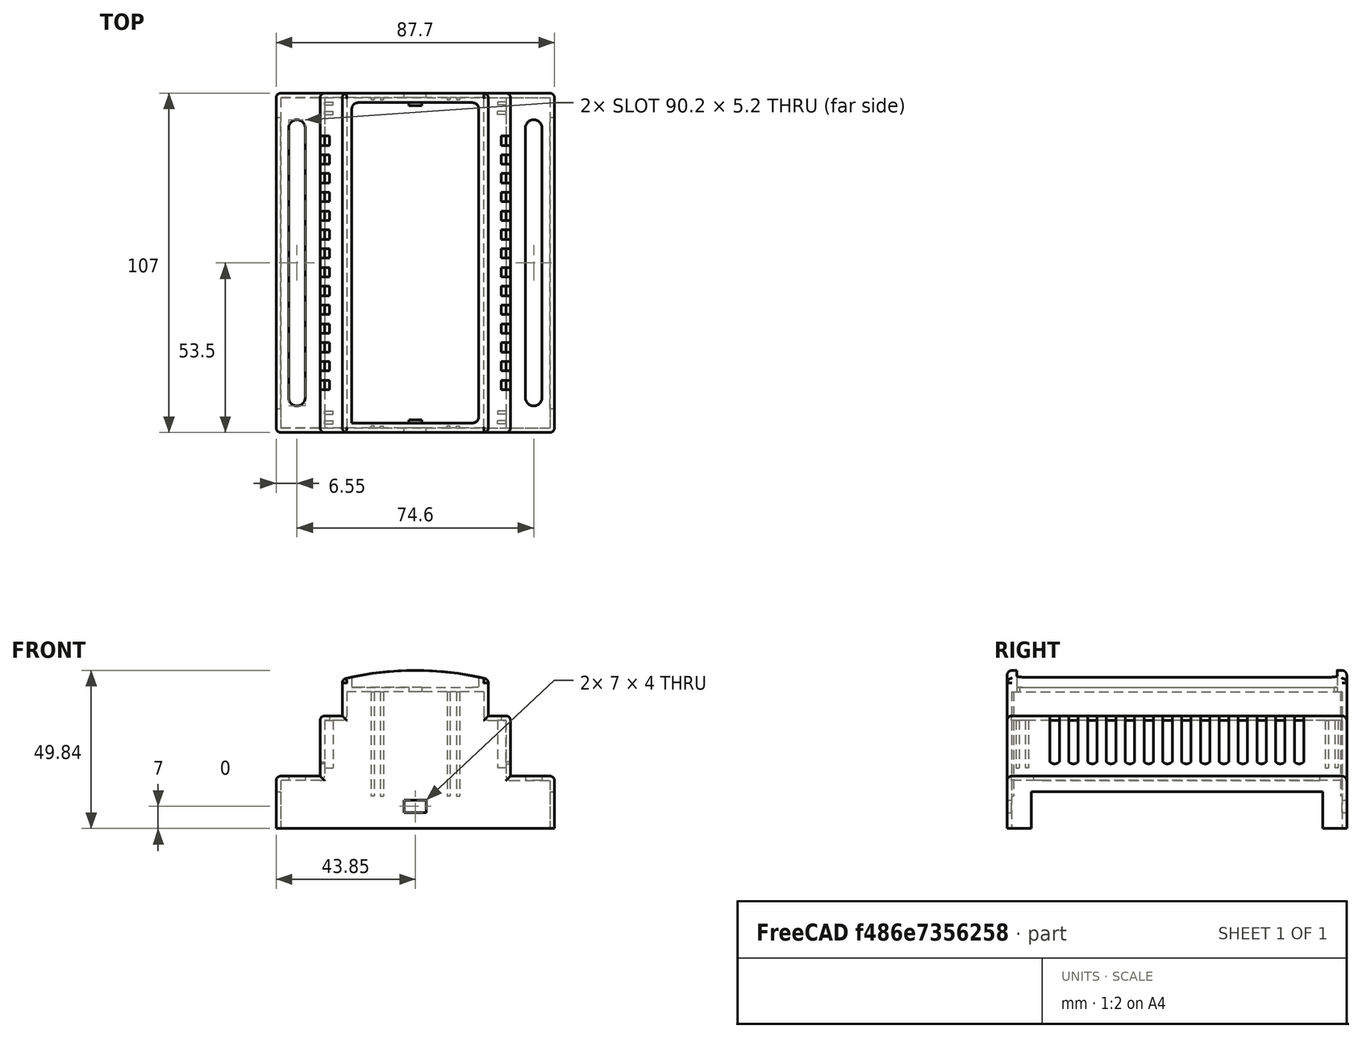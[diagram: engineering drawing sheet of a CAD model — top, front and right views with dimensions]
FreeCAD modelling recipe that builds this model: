
FCSTD DOCUMENT  (FreeCAD 1.0R39109 (Git))
Label: Parte Superior
License: All rights reserved
LicenseURL: https://en.wikipedia.org/wiki/All_rights_reserved
objects: Sketcher::SketchObject×15, PartDesign::Pad×9, PartDesign::Mirrored×7, PartDesign::Pocket×6, PartDesign::Fillet×4, PartDesign::Thickness×2, PartDesign::Plane×1, PartDesign::Body×1
note: 109 computed .brp shape members not serialized (recipe doc carries the construction recipe); baked Part::Feature solids carry a one-line shape summary decoded from their .brp

FEATURE [Sketcher::SketchObject] Sketch
  ArcFitTolerance = 1e-06
  AttachmentSupport = -> [XZ_Plane001]
  FullyConstrained = true
  MakeInternals = false
  MapMode = 5
  Placement = pos=(0,0,0) rot=(1,0,0;1.5708rad)
  sketch-geometry (12):
    g0: LineSegment StartX=-43.85 StartY=0 StartZ=0 EndX=43.85 EndY=0 EndZ=0
    g1: LineSegment StartX=-43.85 StartY=0 StartZ=0 EndX=-43.85 EndY=16.54 EndZ=0
    g2: LineSegment StartX=43.85 StartY=0 StartZ=0 EndX=43.85 EndY=16.54 EndZ=0
    g3: LineSegment StartX=-43.85 StartY=16.54 StartZ=0 EndX=-30 EndY=16.54 EndZ=0
    g4: LineSegment StartX=43.85 StartY=16.54 StartZ=0 EndX=30 EndY=16.54 EndZ=0
    g5: LineSegment StartX=-30 StartY=16.54 StartZ=0 EndX=-30 EndY=35.54 EndZ=0
    g6: LineSegment StartX=30 StartY=16.54 StartZ=0 EndX=30 EndY=35.54 EndZ=0
    g7: LineSegment StartX=-30 StartY=35.54 StartZ=0 EndX=-23 EndY=35.54 EndZ=0
    g8: LineSegment StartX=30 StartY=35.54 StartZ=0 EndX=23 EndY=35.54 EndZ=0
    g9: LineSegment StartX=23 StartY=35.54 StartZ=0 EndX=23 EndY=44.54 EndZ=0
    g10: LineSegment StartX=-23 StartY=35.54 StartZ=0 EndX=-23 EndY=44.54 EndZ=0
    g11: LineSegment StartX=-23 StartY=44.54 StartZ=0 EndX=23 EndY=44.54 EndZ=0
  constraints (36):
    c: Distance(g0) = 87.7
    c: PointOnObject(g0,g-1)
    c: PointOnObject(g0,g-1)
    c: Vertical(g1)
    c: Coincident(g1,g0)
    c: Vertical(g2)
    c: Coincident(g2,g0)
    c: Distance(g3) = 13.85
    c: Horizontal(g3)
    c: Coincident(g3,g1)
    c: Distance(g4) = 13.85
    c: Horizontal(g4)
    c: Coincident(g4,g2)
    c: Vertical(g5)
    c: Coincident(g5,g3)
    c: Vertical(g6)
    c: Coincident(g6,g4)
    c: Distance(g7) = 7
    c: Horizontal(g7)
    c: Coincident(g7,g5)
    c: Distance(g8) = 7
    c: Horizontal(g8)
    c: Coincident(g8,g6)
    c: Vertical(g9)
    c: Coincident(g9,g8)
    c: Vertical(g10)
    c: Coincident(g10,g7)
    c: Coincident(g11,g10)
    c: Coincident(g11,g9)
    c: Equal(g1,g2)
    c: Equal(g5,g6)
    c: Equal(g10,g9)
    c: Distance(g0,g11) = 44.54
    c: DistanceY(g1,g1) = 16.54
    c: Distance(g5,g0) = 35.54
    c: Distance(g10,g-2) = 23
FEATURE [PartDesign::Pad] Pad
  Direction = (0,-1,2e-16)
  Length = 107
  Length2 = 10
  Placement = pos=(0,0,0) rot=(1,0,0;1.5708rad)
  Profile = -> Sketch
  ReferenceAxis = -> Sketch [N_Axis]
  Refine = true
  Suppressed = false
  Type = 0
FEATURE [PartDesign::Thickness] Thickness
  Base = -> Pad
  BaseFeature = -> Pad
  Intersection = false
  Join = 0
  Mode = 0
  Placement = pos=(0,0,0) rot=(1,0,0;1.5708rad)
  Refine = true
  Reversed = true
  SupportTransform = false
  Suppressed = false
  Value = 1.4
FEATURE [PartDesign::Thickness] Thickness001
  Base = -> Thickness [Face1]
  BaseFeature = -> Thickness
  Intersection = false
  Join = 0
  Mode = 0
  Refine = true
  Reversed = true
  SupportTransform = false
  Suppressed = false
  Value = 1.4
FEATURE [Sketcher::SketchObject] Sketch001
  ArcFitTolerance = 1e-06
  AttachmentSupport = -> [Thickness001]
  FullyConstrained = true
  MakeInternals = false
  MapMode = 5
  Placement = pos=(-43.85,0,0) rot=(0.57735,-0.57735,-0.57735;2.0944rad)
  sketch-geometry (4):
    g0: LineSegment StartX=7.575 StartY=0 StartZ=0 EndX=99.425 EndY=0 EndZ=0
    g1: LineSegment StartX=99.425 StartY=0 StartZ=0 EndX=99.425 EndY=11.6 EndZ=0
    g2: LineSegment StartX=99.425 StartY=11.6 StartZ=0 EndX=7.575 EndY=11.6 EndZ=0
    g3: LineSegment StartX=7.575 StartY=11.6 StartZ=0 EndX=7.575 EndY=0 EndZ=0
  constraints (12):
    c: Coincident(g0,g1)
    c: Coincident(g1,g2)
    c: Coincident(g2,g3)
    c: Coincident(g3,g0)
    c: Horizontal(g0)
    c: Horizontal(g2)
    c: Vertical(g1)
    c: Vertical(g3)
    c: PointOnObject(g0,g-1)
    c: DistanceX(g2,g2) = 91.85
    c: DistanceY(g1,g1) = 11.6
    c: DistanceX(g-1,g0) = 7.575
FEATURE [PartDesign::Pocket] Pocket
  BaseFeature = -> Thickness001
  Direction = (1,0,0)
  Length = 5
  Length2 = 5
  Profile = -> Sketch001
  ReferenceAxis = -> Sketch001 [N_Axis]
  Refine = true
  Suppressed = false
  Type = 1
FEATURE [Sketcher::SketchObject] Sketch002
  ArcFitTolerance = 1e-06
  AttachmentSupport = -> [Pocket]
  FullyConstrained = true
  MakeInternals = false
  MapMode = 5
  Placement = pos=(0,4.2e-15,0) rot=(0,0.707107,0.707107;3.14159rad)
  sketch-geometry (4):
    g0: LineSegment StartX=-23 StartY=44.54 StartZ=0 EndX=23 EndY=44.54 EndZ=0
    g1: LineSegment StartX=-23 StartY=44.54 StartZ=0 EndX=-23 EndY=47.04 EndZ=0
    g2: LineSegment StartX=23 StartY=44.54 StartZ=0 EndX=23 EndY=47.04 EndZ=0
    g3: ArcOfCircle CenterX=1.7e-15 CenterY=-46.0243 CenterZ=0 NormalX=0 NormalY=0 NormalZ=1 AngleXU=0 Radius=95.8643 StartAngle=1.32851 EndAngle=1.81308
  constraints (13):
    c: Distance(g0) = 46
    c: Horizontal(g0)
    c: Distance(g-1,g0) = 44.54
    c: Distance(g0,g-2) = 23
    c: Distance(g1) = 2.5
    c: Coincident(g1,g0)
    c: Vertical(g1)
    c: Distance(g2) = 2.5
    c: Coincident(g2,g0)
    c: Vertical(g2)
    c: Coincident(g3,g1)
    c: Coincident(g3,g2)
    c: Distance(g3,g0) = -5.3
FEATURE [PartDesign::Pad] Pad001
  BaseFeature = -> Pocket
  Direction = (0,1,-2e-16)
  Length = 107
  Length2 = 10
  Profile = -> Sketch002
  ReferenceAxis = -> Sketch002 [N_Axis]
  Refine = true
  Suppressed = false
  Type = 0
FEATURE [Sketcher::SketchObject] Sketch003
  ArcFitTolerance = 1e-06
  AttachmentSupport = -> [Pad001]
  ExternalGeometry = -> [Pad001]
  FullyConstrained = true
  MakeInternals = false
  MapMode = 5
  Placement = pos=(0,4.2e-15,0) rot=(0,0.707107,0.707107;3.14159rad)
  sketch-geometry (4):
    g0: LineSegment StartX=-23 StartY=44.54 StartZ=0 EndX=-23 EndY=47.04 EndZ=0
    g1: LineSegment StartX=23 StartY=44.54 StartZ=0 EndX=23 EndY=47.04 EndZ=0
    g2: ArcOfCircle CenterX=4.82e-14 CenterY=-46.0243 CenterZ=0 NormalX=0 NormalY=0 NormalZ=1 AngleXU=0 Radius=95.8643 StartAngle=1.32851 EndAngle=1.81308
    g3: LineSegment StartX=-23 StartY=44.54 StartZ=0 EndX=23 EndY=44.54 EndZ=0
  constraints (9):
    c: Distance(g0) = 2.5
    c: Coincident(g2,g0)
    c: Coincident(g2,g1)
    c: Coincident(g3,g-3)
    c: Coincident(g3,g-3)
    c: Perpendicular(g0,g3) = 4.71239
    c: Distance(g2,g3) = -5.3
    c: Perpendicular(g1,g3) = 4.71239
    c: DistanceY(g1,g1) = 2.5
FEATURE [PartDesign::Pad] Pad002
  BaseFeature = -> Pad001
  Direction = (0,1,-2e-16)
  Length = 3
  Length2 = 10
  Profile = -> Sketch003
  ReferenceAxis = -> Sketch003 [N_Axis]
  Refine = true
  Reversed = true
  Suppressed = false
  Type = 0
FEATURE [Sketcher::SketchObject] Sketch004
  ArcFitTolerance = 1e-06
  AttachmentSupport = -> [Pad002]
  ExternalGeometry = -> [Pad002]
  FullyConstrained = true
  MakeInternals = false
  MapMode = 5
  Placement = pos=(0,-107,0) rot=(1,0,0;1.5708rad)
  sketch-geometry (4):
    g0: LineSegment StartX=-23 StartY=44.54 StartZ=0 EndX=23 EndY=44.54 EndZ=0
    g1: LineSegment StartX=23 StartY=44.54 StartZ=0 EndX=23 EndY=47.04 EndZ=0
    g2: LineSegment StartX=-23 StartY=44.54 StartZ=0 EndX=-23 EndY=47.04 EndZ=0
    g3: ArcOfCircle CenterX=3.7756e-12 CenterY=-46.0243 CenterZ=0 NormalX=0 NormalY=0 NormalZ=1 AngleXU=0 Radius=95.8643 StartAngle=1.32851 EndAngle=1.81308
  constraints (9):
    c: Coincident(g0,g-5)
    c: Coincident(g0,g-6)
    c: Coincident(g1,g0)
    c: Coincident(g1,g-6)
    c: Coincident(g2,g0)
    c: Coincident(g2,g-5)
    c: Coincident(g3,g2)
    c: Coincident(g3,g1)
    c: Tangent(g3,g-4)
FEATURE [PartDesign::Pad] Pad003
  BaseFeature = -> Pad002
  Direction = (0,-1,2e-16)
  Length = 3
  Length2 = 10
  Profile = -> Sketch004
  ReferenceAxis = -> Sketch004 [N_Axis]
  Refine = true
  Reversed = true
  Suppressed = false
  Type = 0
FEATURE [Sketcher::SketchObject] Sketch005
  ArcFitTolerance = 1e-06
  AttachmentSupport = -> [Pad003]
  ExternalGeometry = -> [Pad003]
  FullyConstrained = true
  MakeInternals = false
  MapMode = 5
  Placement = pos=(23,-8.5e-15,1.304e-13) rot=(0.57735,0.57735,0.57735;2.0944rad)
  sketch-geometry (4):
    g0: LineSegment StartX=-104 StartY=49.84 StartZ=0 EndX=-104 EndY=44.54 EndZ=0
    g1: LineSegment StartX=-104 StartY=44.54 StartZ=0 EndX=-3 EndY=44.54 EndZ=0
    g2: LineSegment StartX=-3 StartY=49.84 StartZ=0 EndX=-3 EndY=44.54 EndZ=0
    g3: LineSegment StartX=-104 StartY=49.84 StartZ=0 EndX=-3 EndY=49.84 EndZ=0
  constraints (8):
    c: Coincident(g0,g-5)
    c: Coincident(g0,g-3)
    c: Coincident(g1,g0)
    c: Coincident(g1,g-3)
    c: Coincident(g2,g-4)
    c: Coincident(g2,g1)
    c: Coincident(g3,g0)
    c: Coincident(g3,g2)
FEATURE [PartDesign::Pad] Pad004
  BaseFeature = -> Pad003
  Direction = (1,0,5.8e-15)
  Length = 3
  Length2 = 10
  Profile = -> Sketch005
  ReferenceAxis = -> Sketch005 [N_Axis]
  Refine = true
  Reversed = true
  Suppressed = false
  Type = 0
FEATURE [PartDesign::Mirrored] Mirrored
  BaseFeature = -> Pad004
  MirrorPlane = -> YZ_Plane001
  Originals = -> [Pad004]
  Refine = true
  Suppressed = false
  TransformMode = 0
FEATURE [Sketcher::SketchObject] Sketch006
  ArcFitTolerance = 1e-06
  AttachmentSupport = -> [Mirrored]
  FullyConstrained = true
  MakeInternals = false
  MapMode = 5
  Placement = pos=(0,7.3e-15,16.54) rot=(0,0,1;0rad)
  sketch-geometry (4):
    g0: ArcOfCircle CenterX=37.3 CenterY=-11 CenterZ=0 NormalX=0 NormalY=0 NormalZ=1 AngleXU=0 Radius=2.6 StartAngle=2.2037e-12 EndAngle=3.14159
    g1: ArcOfCircle CenterX=37.3 CenterY=-96 CenterZ=0 NormalX=0 NormalY=0 NormalZ=1 AngleXU=0 Radius=2.6 StartAngle=3.14159 EndAngle=6.28319
    g2: LineSegment StartX=39.9 StartY=-11 StartZ=0 EndX=39.9 EndY=-96 EndZ=0
    g3: LineSegment StartX=34.7 StartY=-11 StartZ=0 EndX=34.7 EndY=-96 EndZ=0
  constraints (10):
    c: Tangent(g0,g2) = 1.5708
    c: Tangent(g0,g3) = -1.5708
    c: Tangent(g1,g2) = 1.5708
    c: Tangent(g1,g3) = -1.5708
    c: Equal(g0,g1)
    c: Vertical(g2)
    c: Distance(g2,g3) = 5.2
    c: DistanceY(g2,g2) = 85
    c: Distance(g0,g-2) = 37.3
    c: Distance(g0,g-1) = 11
FEATURE [PartDesign::Pocket] Pocket001
  BaseFeature = -> Mirrored
  Direction = (0,0,-1)
  Length = 5
  Length2 = 5
  Profile = -> Sketch006
  ReferenceAxis = -> Sketch006 [N_Axis]
  Refine = true
  Suppressed = false
  Type = 0
FEATURE [PartDesign::Mirrored] Mirrored001
  BaseFeature = -> Pocket001
  MirrorPlane = -> YZ_Plane001
  Originals = -> [Pocket001]
  Refine = true
  Suppressed = false
  TransformMode = 0
FEATURE [Sketcher::SketchObject] Sketch007
  ArcFitTolerance = 1e-06
  AttachmentSupport = -> [Mirrored001]
  ExternalGeometry = -> [Mirrored001]
  FullyConstrained = true
  MakeInternals = false
  MapMode = 5
  Placement = pos=(30,0,0) rot=(0.57735,0.57735,0.57735;2.0944rad)
  sketch-geometry (57):
    g0: LineSegment [constr] StartX=-53.5 StartY=35.54 StartZ=0 EndX=-53.5 EndY=16.54 EndZ=0
    g1: LineSegment StartX=-16.4625 StartY=35.54 StartZ=0 EndX=-13.4995 EndY=35.54 EndZ=0
    g2: LineSegment StartX=-13.4995 StartY=35.54 StartZ=0 EndX=-13.4995 EndY=21.04 EndZ=0
    g3: LineSegment StartX=-16.4625 StartY=35.54 StartZ=0 EndX=-16.4625 EndY=21.04 EndZ=0
    g4: ArcOfCircle CenterX=-14.981 CenterY=22.3836 CenterZ=0 NormalX=0 NormalY=0 NormalZ=1 AngleXU=0 Radius=2 StartAngle=3.8782 EndAngle=5.54658
    g5: LineSegment StartX=-22.3885 StartY=35.54 StartZ=0 EndX=-19.4255 EndY=35.54 EndZ=0
    g6: LineSegment StartX=-19.4255 StartY=35.54 StartZ=0 EndX=-19.4255 EndY=21.04 EndZ=0
    g7: LineSegment StartX=-22.3885 StartY=35.54 StartZ=0 EndX=-22.3885 EndY=21.04 EndZ=0
    g8: ArcOfCircle CenterX=-20.907 CenterY=22.3836 CenterZ=0 NormalX=0 NormalY=0 NormalZ=1 AngleXU=0 Radius=2 StartAngle=3.8782 EndAngle=5.54658
    g9: LineSegment StartX=-28.3145 StartY=35.54 StartZ=0 EndX=-25.3515 EndY=35.54 EndZ=0
    g10: LineSegment StartX=-25.3515 StartY=35.54 StartZ=0 EndX=-25.3515 EndY=21.04 EndZ=0
    g11: LineSegment StartX=-28.3145 StartY=35.54 StartZ=0 EndX=-28.3145 EndY=21.04 EndZ=0
    g12: ArcOfCircle CenterX=-26.833 CenterY=22.3836 CenterZ=0 NormalX=0 NormalY=0 NormalZ=1 AngleXU=0 Radius=2 StartAngle=3.8782 EndAngle=5.54658
    g13: LineSegment StartX=-34.2405 StartY=35.54 StartZ=0 EndX=-31.2775 EndY=35.54 EndZ=0
    g14: LineSegment StartX=-34.2405 StartY=35.54 StartZ=0 EndX=-34.2405 EndY=21.04 EndZ=0
    g15: LineSegment StartX=-31.2775 StartY=35.54 StartZ=0 EndX=-31.2775 EndY=21.04 EndZ=0
    g16: ArcOfCircle CenterX=-32.759 CenterY=22.3836 CenterZ=0 NormalX=0 NormalY=0 NormalZ=1 AngleXU=0 Radius=2 StartAngle=3.8782 EndAngle=5.54658
    g17: LineSegment StartX=-40.1665 StartY=35.54 StartZ=0 EndX=-37.2035 EndY=35.54 EndZ=0
    g18: LineSegment StartX=-37.2035 StartY=35.54 StartZ=0 EndX=-37.2035 EndY=21.04 EndZ=0
    g19: LineSegment StartX=-40.1665 StartY=35.54 StartZ=0 EndX=-40.1665 EndY=21.04 EndZ=0
    g20: ArcOfCircle CenterX=-38.685 CenterY=22.3836 CenterZ=0 NormalX=0 NormalY=0 NormalZ=1 AngleXU=0 Radius=2 StartAngle=3.8782 EndAngle=5.54658
    g21: LineSegment StartX=-46.0925 StartY=35.54 StartZ=0 EndX=-43.1295 EndY=35.54 EndZ=0
    g22: LineSegment StartX=-43.1295 StartY=35.54 StartZ=0 EndX=-43.1295 EndY=21.04 EndZ=0
    g23: LineSegment StartX=-46.0925 StartY=35.54 StartZ=0 EndX=-46.0925 EndY=21.04 EndZ=0
    g24: ArcOfCircle CenterX=-44.611 CenterY=22.3836 CenterZ=0 NormalX=0 NormalY=0 NormalZ=1 AngleXU=0 Radius=2 StartAngle=3.8782 EndAngle=5.54658
    g25: LineSegment StartX=-52.0185 StartY=35.54 StartZ=0 EndX=-49.0555 EndY=35.54 EndZ=0
    g26: LineSegment StartX=-49.0555 StartY=35.54 StartZ=0 EndX=-49.0555 EndY=21.04 EndZ=0
    g27: LineSegment StartX=-52.0185 StartY=35.54 StartZ=0 EndX=-52.0185 EndY=21.04 EndZ=0
    g28: ArcOfCircle CenterX=-50.537 CenterY=22.3836 CenterZ=0 NormalX=0 NormalY=0 NormalZ=1 AngleXU=0 Radius=2 StartAngle=3.8782 EndAngle=5.54658
    g29: LineSegment StartX=-57.9445 StartY=35.54 StartZ=0 EndX=-54.9815 EndY=35.54 EndZ=0
    g30: LineSegment StartX=-54.9815 StartY=35.54 StartZ=0 EndX=-54.9815 EndY=21.04 EndZ=0
    g31: LineSegment StartX=-57.9445 StartY=35.54 StartZ=0 EndX=-57.9445 EndY=21.04 EndZ=0
    g32: ArcOfCircle CenterX=-56.463 CenterY=22.3836 CenterZ=0 NormalX=0 NormalY=0 NormalZ=1 AngleXU=0 Radius=2 StartAngle=3.8782 EndAngle=5.54658
    g33: LineSegment StartX=-63.8705 StartY=35.54 StartZ=0 EndX=-60.9075 EndY=35.54 EndZ=0
    g34: LineSegment StartX=-60.9075 StartY=35.54 StartZ=0 EndX=-60.9075 EndY=21.04 EndZ=0
    g35: LineSegment StartX=-63.8705 StartY=35.54 StartZ=0 EndX=-63.8705 EndY=21.04 EndZ=0
    g36: ArcOfCircle CenterX=-62.389 CenterY=22.3836 CenterZ=0 NormalX=0 NormalY=0 NormalZ=1 AngleXU=0 Radius=2 StartAngle=3.8782 EndAngle=5.54658
    g37: LineSegment StartX=-69.7965 StartY=35.54 StartZ=0 EndX=-66.8335 EndY=35.54 EndZ=0
    g38: LineSegment StartX=-66.8335 StartY=35.54 StartZ=0 EndX=-66.8335 EndY=21.04 EndZ=0
    g39: LineSegment StartX=-69.7965 StartY=35.54 StartZ=0 EndX=-69.7965 EndY=21.04 EndZ=0
    g40: ArcOfCircle CenterX=-68.315 CenterY=22.3836 CenterZ=0 NormalX=0 NormalY=0 NormalZ=1 AngleXU=0 Radius=2 StartAngle=3.8782 EndAngle=5.54658
    g41: LineSegment StartX=-75.7225 StartY=35.54 StartZ=0 EndX=-72.7595 EndY=35.54 EndZ=0
    g42: LineSegment StartX=-72.7595 StartY=35.54 StartZ=0 EndX=-72.7595 EndY=21.04 EndZ=0
    g43: LineSegment StartX=-75.7225 StartY=35.54 StartZ=0 EndX=-75.7225 EndY=21.04 EndZ=0
    g44: ArcOfCircle CenterX=-74.241 CenterY=22.3836 CenterZ=0 NormalX=0 NormalY=0 NormalZ=1 AngleXU=0 Radius=2 StartAngle=3.8782 EndAngle=5.54658
    g45: LineSegment StartX=-81.6485 StartY=35.54 StartZ=0 EndX=-78.6855 EndY=35.54 EndZ=0
    g46: LineSegment StartX=-78.6855 StartY=35.54 StartZ=0 EndX=-78.6855 EndY=21.04 EndZ=0
    g47: LineSegment StartX=-81.6485 StartY=35.54 StartZ=0 EndX=-81.6485 EndY=21.04 EndZ=0
    g48: ArcOfCircle CenterX=-80.167 CenterY=22.3836 CenterZ=0 NormalX=0 NormalY=0 NormalZ=1 AngleXU=0 Radius=2 StartAngle=3.8782 EndAngle=5.54658
    g49: LineSegment StartX=-87.5745 StartY=35.54 StartZ=0 EndX=-84.6115 EndY=35.54 EndZ=0
    g50: LineSegment StartX=-84.6115 StartY=35.54 StartZ=0 EndX=-84.6115 EndY=21.04 EndZ=0
    g51: LineSegment StartX=-87.5745 StartY=35.54 StartZ=0 EndX=-87.5745 EndY=21.04 EndZ=0
    g52: ArcOfCircle CenterX=-86.093 CenterY=22.3836 CenterZ=0 NormalX=0 NormalY=0 NormalZ=1 AngleXU=0 Radius=2 StartAngle=3.8782 EndAngle=5.54658
    g53: LineSegment StartX=-93.5005 StartY=35.54 StartZ=0 EndX=-90.5375 EndY=35.54 EndZ=0
    g54: LineSegment StartX=-90.5375 StartY=35.54 StartZ=0 EndX=-90.5375 EndY=21.04 EndZ=0
    g55: LineSegment StartX=-93.5005 StartY=35.54 StartZ=0 EndX=-93.5005 EndY=21.04 EndZ=0
    g56: ArcOfCircle CenterX=-92.019 CenterY=22.3836 CenterZ=0 NormalX=0 NormalY=0 NormalZ=1 AngleXU=0 Radius=2 StartAngle=3.8782 EndAngle=5.54658
  constraints (184):
    c: Symmetric(g-4,g-4,g0)
    c: Symmetric(g-3,g-3,g0)
    c: PointOnObject(g1,g-4)
    c: PointOnObject(g1,g-4)
    c: Distance(g2) = 14.5
    c: Vertical(g2)
    c: Coincident(g2,g1)
    c: Vertical(g3)
    c: Coincident(g3,g1)
    c: Coincident(g4,g3)
    c: Coincident(g4,g2)
    c: DistanceX(g1,g1) = 2.963
    c: Radius(g4) = 2
    c: Distance(g5) = 2.963
    c: Horizontal(g5)
    c: PointOnObject(g5,g-4)
    c: Vertical(g6)
    c: Coincident(g6,g5)
    c: Vertical(g7)
    c: Coincident(g7,g5)
    c: Equal(g2,g3)
    c: Equal(g3,g6)
    c: Equal(g6,g7)
    c: Distance(g3,g6) = 2.963
    c: Coincident(g8,g7)
    c: Coincident(g8,g6)
    c: Equal(g4,g8)
    c: Horizontal(g9)
    c: PointOnObject(g9,g-4)
    c: Vertical(g10)
    c: Coincident(g10,g9)
    c: Vertical(g11)
    c: Coincident(g11,g9)
    c: Coincident(g12,g11)
    c: Coincident(g12,g10)
    c: Equal(g5,g9)
    c: Equal(g6,g10)
    c: Equal(g10,g11)
    c: Equal(g4,g12)
    c: Distance(g7,g10) = 2.963
    c: PointOnObject(g13,g-4)
    c: PointOnObject(g13,g-4)
    c: Vertical(g14)
    c: Coincident(g14,g13)
    c: Vertical(g15)
    c: Coincident(g15,g13)
    c: Coincident(g16,g14)
    c: Coincident(g16,g15)
    c: Equal(g15,g14)
    c: Equal(g14,g2)
    c: Equal(g1,g13)
    c: Distance(g11,g15) = 2.963
    c: Equal(g4,g16)
    c: PointOnObject(g17,g-4)
    c: PointOnObject(g17,g-4)
    c: Vertical(g18)
    c: Coincident(g18,g17)
    c: Vertical(g19)
    c: Coincident(g19,g17)
    c: Coincident(g20,g19)
    c: Coincident(g20,g18)
    c: Distance(g14,g18) = 2.963
    c: Equal(g2,g18)
    c: Equal(g18,g19)
    c: Equal(g1,g17)
    c: Equal(g4,g20)
    c: PointOnObject(g21,g-4)
    c: PointOnObject(g21,g-4)
    c: Vertical(g22)
    c: Coincident(g22,g21)
    c: Vertical(g23)
    c: Coincident(g23,g21)
    c: Coincident(g24,g23)
    c: Coincident(g24,g22)
    c: Equal(g1,g21)
    c: Equal(g22,g23)
    c: Equal(g23,g2)
    c: Distance(g19,g22) = 2.963
    c: Equal(g4,g24)
    c: PointOnObject(g25,g-4)
    c: PointOnObject(g25,g-4)
    c: Vertical(g26)
    c: Coincident(g26,g25)
    c: Vertical(g27)
    c: Coincident(g27,g25)
    c: Coincident(g28,g27)
    c: Coincident(g28,g26)
    c: Equal(g2,g26)
    c: Equal(g26,g27)
    c: Equal(g1,g25)
    c: Equal(g4,g28)
    c: Distance(g23,g26) = 2.963
    c: PointOnObject(g29,g-4)
    c: PointOnObject(g29,g-4)
    c: Coincident(g30,g29)
    c: Vertical(g30)
    c: Coincident(g31,g29)
    c: Vertical(g31)
    c: Equal(g30,g31)
    c: Equal(g31,g3)
    c: Coincident(g32,g31)
    c: Coincident(g32,g30)
    c: Equal(g4,g32)
    c: Equal(g29,g1)
    c: Distance(g27,g30) = 2.963
    c: PointOnObject(g33,g-4)
    c: PointOnObject(g33,g-4)
    c: Coincident(g34,g33)
    c: Vertical(g34)
    c: Coincident(g35,g33)
    c: Vertical(g35)
    c: Equal(g35,g34)
    c: Equal(g34,g31)
    c: Equal(g33,g29)
    c: Coincident(g36,g35)
    c: Coincident(g36,g34)
    c: Equal(g32,g36)
    c: Distance(g31,g34) = 2.963
    c: PointOnObject(g37,g-4)
    c: PointOnObject(g37,g-4)
    c: Coincident(g38,g37)
    c: Vertical(g38)
    c: Coincident(g39,g37)
    c: Vertical(g39)
    c: Coincident(g40,g39)
    c: Coincident(g40,g38)
    c: Equal(g38,g39)
    c: Equal(g39,g35)
    c: Equal(g40,g36)
    c: Equal(g33,g37)
    c: Distance(g35,g38) = 2.963
    c: PointOnObject(g41,g-4)
    c: PointOnObject(g41,g-4)
    c: Coincident(g42,g41)
    c: Vertical(g42)
    c: Coincident(g43,g41)
    c: Vertical(g43)
    c: Coincident(g44,g43)
    c: Coincident(g44,g42)
    c: Equal(g43,g42)
    c: Equal(g42,g39)
    c: Equal(g41,g37)
    c: Equal(g44,g40)
    c: Distance(g39,g42) = 2.963
    c: PointOnObject(g45,g-4)
    c: PointOnObject(g45,g-4)
    c: Coincident(g46,g45)
    c: Vertical(g46)
    c: Coincident(g47,g45)
    c: Vertical(g47)
    c: Coincident(g48,g47)
    c: Coincident(g48,g46)
    c: Equal(g47,g46)
    c: Equal(g46,g43)
    c: Equal(g45,g41)
    c: Equal(g44,g48)
    c: Distance(g43,g46) = 2.963
    c: PointOnObject(g49,g-4)
    c: PointOnObject(g49,g-4)
    c: Coincident(g50,g49)
    c: Vertical(g50)
    c: Coincident(g51,g49)
    c: Vertical(g51)
    c: Coincident(g52,g51)
    c: Coincident(g52,g50)
    c: Equal(g51,g50)
    c: Equal(g50,g47)
    c: Equal(g49,g45)
    c: Equal(g48,g52)
    c: Distance(g47,g50) = 2.963
    c: PointOnObject(g53,g-4)
    c: PointOnObject(g53,g-4)
    c: Coincident(g54,g53)
    c: Vertical(g54)
    c: Coincident(g55,g53)
    c: Vertical(g55)
    c: Coincident(g56,g55)
    c: Coincident(g56,g54)
    c: Equal(g55,g54)
    c: Equal(g54,g51)
    c: Equal(g56,g52)
    c: Equal(g53,g49)
    c: Distance(g51,g54) = 2.963
    c: Distance(g0,g27) = 1.4815
FEATURE [PartDesign::Pocket] Pocket002
  BaseFeature = -> Mirrored001
  Direction = (-1,0,0)
  Length = 2.963
  Length2 = 5
  Profile = -> Sketch007
  ReferenceAxis = -> Sketch007 [N_Axis]
  Refine = true
  Suppressed = false
  Type = 0
FEATURE [PartDesign::Mirrored] Mirrored002
  BaseFeature = -> Pocket002
  MirrorPlane = -> YZ_Plane001
  Originals = -> [Pocket002]
  Refine = true
  Suppressed = false
  TransformMode = 0
FEATURE [PartDesign::Fillet] Fillet
  Base = -> Mirrored002 [Edge272,Edge110,Edge99,Edge166,Edge114,Edge118,Edge122,Edge126,Edge130,Edge134,Edge138,Edge142,Edge146,Edge150,Edge154,Edge158,Edge162,Edge20,Edge98,Edge97,Edge96]
  BaseFeature = -> Mirrored002
  Radius = 1.5
  Refine = true
  SupportTransform = false
  Suppressed = false
  UseAllEdges = false
FEATURE [PartDesign::Mirrored] Mirrored003
  BaseFeature = -> Fillet
  MirrorPlane = -> YZ_Plane001
  Originals = -> [Fillet]
  Refine = true
  Suppressed = false
  TransformMode = 0
FEATURE [Sketcher::SketchObject] Sketch008
  ArcFitTolerance = 1e-06
  AttachmentSupport = -> [Mirrored003]
  FullyConstrained = true
  MakeInternals = false
  MapMode = 5
  Placement = pos=(0,-107,3.53e-14) rot=(1,0,0;1.5708rad)
  sketch-geometry (4):
    g0: LineSegment StartX=-3.5 StartY=9 StartZ=0 EndX=3.5 EndY=9 EndZ=0
    g1: LineSegment StartX=-3.5 StartY=9 StartZ=0 EndX=-3.5 EndY=5 EndZ=0
    g2: LineSegment StartX=3.5 StartY=9 StartZ=0 EndX=3.5 EndY=5 EndZ=0
    g3: LineSegment StartX=-3.5 StartY=5 StartZ=0 EndX=3.5 EndY=5 EndZ=0
  constraints (12):
    c: Distance(g0) = 7
    c: Horizontal(g0)
    c: Vertical(g1)
    c: Coincident(g1,g0)
    c: Distance(g2) = 4
    c: Vertical(g2)
    c: Coincident(g2,g0)
    c: Coincident(g3,g1)
    c: Coincident(g3,g2)
    c: Distance(g-2,g1) = 3.5
    c: Equal(g2,g1)
    c: Distance(g-1,g3) = 5
FEATURE [PartDesign::Pocket] Pocket003
  BaseFeature = -> Mirrored003
  Direction = (0,1,-2e-16)
  Length = 5
  Length2 = 5
  Profile = -> Sketch008
  ReferenceAxis = -> Sketch008 [N_Axis]
  Refine = true
  Suppressed = false
  Type = 1
FEATURE [Sketcher::SketchObject] Sketch009
  ArcFitTolerance = 1e-06
  AttachmentSupport = -> [Pocket003]
  ExternalGeometry = -> [Pocket003]
  FullyConstrained = true
  MakeInternals = false
  MapMode = 5
  Placement = pos=(0,-104,0) rot=(1,0,0;1.5708rad)
  sketch-geometry (8):
    g0: LineSegment StartX=-23 StartY=47.04 StartZ=0 EndX=-23 EndY=49.84 EndZ=0
    g1: LineSegment StartX=-23 StartY=49.84 StartZ=0 EndX=-20 EndY=49.84 EndZ=0
    g2: LineSegment StartX=-20 StartY=49.84 StartZ=0 EndX=-20 EndY=47.7305 EndZ=0
    g3: ArcOfCircle CenterX=9.71783e-05 CenterY=-46.0247 CenterZ=0 NormalX=0 NormalY=0 NormalZ=1 AngleXU=0 Radius=95.8647 StartAngle=1.78097 EndAngle=1.81308
    g4: LineSegment StartX=20 StartY=49.84 StartZ=0 EndX=23 EndY=49.84 EndZ=0
    g5: LineSegment StartX=23 StartY=49.84 StartZ=0 EndX=23 EndY=47.04 EndZ=0
    g6: LineSegment StartX=20 StartY=49.84 StartZ=0 EndX=20 EndY=47.7305 EndZ=0
    g7: ArcOfCircle CenterX=-7.58465e-05 CenterY=-46.0246 CenterZ=0 NormalX=0 NormalY=0 NormalZ=1 AngleXU=0 Radius=95.8646 StartAngle=1.32851 EndAngle=1.36062
  constraints (19):
    c: Coincident(g0,g-6)
    c: Coincident(g0,g-6)
    c: Coincident(g1,g0)
    c: Coincident(g1,g-5)
    c: Coincident(g2,g1)
    c: Coincident(g2,g-4)
    c: Coincident(g3,g0)
    c: Coincident(g3,g2)
    c: Tangent(g3,g-3)
    c: Coincident(g4,g-8)
    c: Coincident(g4,g-9)
    c: Coincident(g5,g4)
    c: PointOnObject(g5,g-10)
    c: Vertical(g5)
    c: Coincident(g6,g4)
    c: Coincident(g6,g-10)
    c: Coincident(g7,g6)
    c: Coincident(g7,g5)
    c: Tangent(g7,g-10)
FEATURE [PartDesign::Pocket] Pocket004
  BaseFeature = -> Pocket003
  Direction = (0,1,-2e-16)
  Length = 0
  Length2 = 5
  Profile = -> Sketch009
  ReferenceAxis = -> Sketch009 [N_Axis]
  Refine = true
  Suppressed = false
  Type = 3
  UpToFace = -> Pocket003 [Face89]
FEATURE [PartDesign::Mirrored] Mirrored004
  BaseFeature = -> Pocket004
  MirrorPlane = -> YZ_Plane001
  Originals = -> [Fillet]
  Refine = true
  Suppressed = false
  TransformMode = 0
FEATURE [PartDesign::Fillet] Fillet001
  Base = -> Mirrored004 [Edge26,Edge28,Edge32,Edge34,Edge33,Edge5,Edge22,Edge24,Edge25,Edge29]
  BaseFeature = -> Mirrored004
  Radius = 1.5
  Refine = true
  SupportTransform = false
  Suppressed = false
  UseAllEdges = false
FEATURE [Sketcher::SketchObject] Sketch010
  ArcFitTolerance = 1e-06
  FullyConstrained = true
  MakeInternals = false
  MapMode = 5
  Placement = pos=(0,1.96e-14,44.54) rot=(0,0,1;0rad)
  sketch-geometry (8):
    g0: LineSegment StartX=-2 StartY=-3 StartZ=0 EndX=2 EndY=-3 EndZ=0
    g1: LineSegment StartX=-2 StartY=-3 StartZ=0 EndX=-2 EndY=-4 EndZ=0
    g2: LineSegment StartX=2 StartY=-3 StartZ=0 EndX=2 EndY=-4 EndZ=0
    g3: LineSegment StartX=-2 StartY=-4 StartZ=0 EndX=2 EndY=-4 EndZ=0
    g4: LineSegment StartX=2 StartY=-104 StartZ=0 EndX=-2 EndY=-104 EndZ=0
    g5: LineSegment StartX=2 StartY=-104 StartZ=0 EndX=2 EndY=-103 EndZ=0
    g6: LineSegment StartX=-2 StartY=-104 StartZ=0 EndX=-2 EndY=-103 EndZ=0
    g7: LineSegment StartX=2 StartY=-103 StartZ=0 EndX=-2 EndY=-103 EndZ=0
  constraints (24):
    c: PointOnObject(g0,g-3)
    c: PointOnObject(g0,g-3)
    c: Distance(g1) = 1
    c: Vertical(g1)
    c: Coincident(g1,g0)
    c: Distance(g2) = 1
    c: Vertical(g2)
    c: Coincident(g2,g0)
    c: Coincident(g3,g1)
    c: Coincident(g3,g2)
    c: Distance(g-2,g1) = 2
    c: Distance(g0,g0) = 4
    c: PointOnObject(g4,g-4)
    c: PointOnObject(g4,g-4)
    c: Distance(g5) = 1
    c: Vertical(g5)
    c: Coincident(g5,g4)
    c: Distance(g6) = 1
    c: Vertical(g6)
    c: Coincident(g6,g4)
    c: Coincident(g7,g5)
    c: Coincident(g7,g6)
    c: Distance(g-2,g5) = 2
    c: DistanceX(g4,g4) = 4
FEATURE [PartDesign::Pocket] Pocket005
  BaseFeature = -> Fillet001
  Direction = (0,0,-1)
  Length = 5
  Length2 = 5
  Profile = -> Sketch010
  ReferenceAxis = -> Sketch010 [N_Axis]
  Refine = true
  Suppressed = false
  Type = 0
FEATURE [PartDesign::Fillet] Fillet002
  Base = -> Pocket005 [Edge3,Edge78,Edge86,Edge10]
  BaseFeature = -> Pocket005
  Radius = 1.5
  Refine = true
  SupportTransform = false
  Suppressed = false
  UseAllEdges = false
FEATURE [Sketcher::SketchObject] Sketch011
  ArcFitTolerance = 1e-06
  FullyConstrained = true
  MakeInternals = false
  MapMode = 5
  Placement = pos=(0,-105.6,0) rot=(0,0.707107,0.707107;3.14159rad)
  sketch-geometry (9):
    g0: LineSegment [constr] StartX=-12 StartY=43.14 StartZ=0 EndX=-12 EndY=10.2 EndZ=0
    g1: LineSegment StartX=-11 StartY=43.14 StartZ=0 EndX=-11 EndY=10.2 EndZ=0
    g2: LineSegment StartX=-10 StartY=43.14 StartZ=0 EndX=-10 EndY=10.2 EndZ=0
    g3: LineSegment StartX=-11 StartY=10.2 StartZ=0 EndX=-10 EndY=10.2 EndZ=0
    g4: LineSegment StartX=-11 StartY=43.14 StartZ=0 EndX=-10 EndY=43.14 EndZ=0
    g5: LineSegment StartX=-13 StartY=43.14 StartZ=0 EndX=-13 EndY=10.2 EndZ=0
    g6: LineSegment StartX=-14 StartY=43.14 StartZ=0 EndX=-14 EndY=10.2 EndZ=0
    g7: LineSegment StartX=-13 StartY=10.2 StartZ=0 EndX=-14 EndY=10.2 EndZ=0
    g8: LineSegment StartX=-13 StartY=43.14 StartZ=0 EndX=-14 EndY=43.14 EndZ=0
  constraints (25):
    c: Distance(g0) = 32.94
    c: Vertical(g0)
    c: PointOnObject(g0,g-3)
    c: Distance(g-2,g0) = 12
    c: PointOnObject(g1,g-3)
    c: Vertical(g1)
    c: PointOnObject(g2,g-3)
    c: Vertical(g2)
    c: Equal(g2,g0)
    c: Distance(g3) = 1
    c: Coincident(g3,g1)
    c: Perpendicular(g2,g3) = 1.5708
    c: Coincident(g4,g1)
    c: Coincident(g4,g2)
    c: Distance(g1,g0) = 1
    c: Vertical(g5)
    c: Vertical(g6)
    c: Distance(g7) = 1
    c: Coincident(g7,g5)
    c: Perpendicular(g6,g7) = 4.71239
    c: Coincident(g8,g5)
    c: Coincident(g8,g6)
    c: Symmetric(g1,g5,g0)
    c: Equal(g0,g1)
    c: Equal(g6,g0)
FEATURE [PartDesign::Pad] Pad005
  BaseFeature = -> Fillet002
  Direction = (0,1,-2e-16)
  Length = 0.63
  Length2 = 10
  Profile = -> Sketch011
  ReferenceAxis = -> Sketch011 [N_Axis]
  Refine = true
  Suppressed = false
  Type = 0
FEATURE [PartDesign::Mirrored] Mirrored005
  BaseFeature = -> Pad005
  MirrorPlane = -> YZ_Plane001
  Originals = -> [Pad005]
  Refine = true
  Suppressed = false
  TransformMode = 0
FEATURE [Sketcher::SketchObject] Sketch012
  ArcFitTolerance = 1e-06
  AttachmentSupport = -> [Mirrored005]
  ExternalGeometry = -> [Mirrored005]
  FullyConstrained = true
  MakeInternals = false
  MapMode = 5
  Placement = pos=(0,-1.4,0) rot=(1,0,0;1.5708rad)
  sketch-geometry (16):
    g0: LineSegment StartX=-14 StartY=43.14 StartZ=0 EndX=-13 EndY=43.14 EndZ=0
    g1: LineSegment StartX=-11 StartY=43.14 StartZ=0 EndX=-10 EndY=43.14 EndZ=0
    g2: LineSegment StartX=-14 StartY=43.14 StartZ=0 EndX=-14 EndY=10.2 EndZ=0
    g3: LineSegment StartX=-14 StartY=10.2 StartZ=0 EndX=-13 EndY=10.2 EndZ=0
    g4: LineSegment StartX=-13 StartY=10.2 StartZ=0 EndX=-13 EndY=43.14 EndZ=0
    g5: LineSegment StartX=-11 StartY=43.14 StartZ=0 EndX=-11 EndY=10.2 EndZ=0
    g6: LineSegment StartX=-11 StartY=10.2 StartZ=0 EndX=-10 EndY=10.2 EndZ=0
    g7: LineSegment StartX=-10 StartY=10.2 StartZ=0 EndX=-10 EndY=43.14 EndZ=0
    g8: LineSegment StartX=10 StartY=43.14 StartZ=0 EndX=11 EndY=43.14 EndZ=0
    g9: LineSegment StartX=10 StartY=43.14 StartZ=0 EndX=10 EndY=10.2 EndZ=0
    g10: LineSegment StartX=10 StartY=10.2 StartZ=0 EndX=11 EndY=10.2 EndZ=0
    g11: LineSegment StartX=11 StartY=10.2 StartZ=0 EndX=11 EndY=43.14 EndZ=0
    g12: LineSegment StartX=13 StartY=43.14 StartZ=0 EndX=14 EndY=43.14 EndZ=0
    g13: LineSegment StartX=13 StartY=43.14 StartZ=0 EndX=13 EndY=10.2 EndZ=0
    g14: LineSegment StartX=13 StartY=10.2 StartZ=0 EndX=14 EndY=10.2 EndZ=0
    g15: LineSegment StartX=14 StartY=10.2 StartZ=0 EndX=14 EndY=43.14 EndZ=0
  constraints (32):
    c: Coincident(g0,g-16)
    c: Coincident(g0,g-15)
    c: Coincident(g1,g-13)
    c: Coincident(g1,g-14)
    c: Coincident(g2,g0)
    c: Coincident(g2,g-18)
    c: Coincident(g3,g2)
    c: Coincident(g3,g-18)
    c: Coincident(g4,g3)
    c: Coincident(g4,g0)
    c: Coincident(g5,g1)
    c: Coincident(g5,g-17)
    c: Coincident(g6,g5)
    c: Coincident(g6,g-17)
    c: Coincident(g7,g6)
    c: Coincident(g7,g1)
    c: Coincident(g8,g-7)
    c: Coincident(g8,g-8)
    c: Coincident(g9,g8)
    c: Coincident(g9,g-10)
    c: Coincident(g10,g9)
    c: Coincident(g10,g-10)
    c: Coincident(g11,g10)
    c: Coincident(g11,g8)
    c: Coincident(g12,g-5)
    c: Coincident(g12,g-5)
    c: Coincident(g13,g12)
    c: Coincident(g13,g-9)
    c: Coincident(g14,g13)
    c: Coincident(g14,g-9)
    c: Coincident(g15,g14)
    c: Coincident(g15,g12)
FEATURE [PartDesign::Pad] Pad006
  BaseFeature = -> Mirrored005
  Direction = (0,-1,2e-16)
  Length = 0.63
  Length2 = 10
  Profile = -> Sketch012
  ReferenceAxis = -> Sketch012 [N_Axis]
  Refine = true
  Suppressed = false
  Type = 0
FEATURE [Sketcher::SketchObject] Sketch013
  ArcFitTolerance = 1e-06
  AttachmentSupport = -> [Pad006]
  ExternalGeometry = -> [Pad006]
  FullyConstrained = true
  MakeInternals = false
  MapMode = 5
  Placement = pos=(28.6,0,0) rot=(0.57735,-0.57735,-0.57735;2.0944rad)
  sketch-geometry (9):
    g0: LineSegment [constr] StartX=4.76 StartY=34.14 StartZ=0 EndX=4.76 EndY=19.14 EndZ=0
    g1: LineSegment StartX=2.76 StartY=34.14 StartZ=0 EndX=3.76 EndY=34.14 EndZ=0
    g2: LineSegment StartX=2.76 StartY=34.14 StartZ=0 EndX=2.76 EndY=19.14 EndZ=0
    g3: LineSegment StartX=3.76 StartY=34.14 StartZ=0 EndX=3.76 EndY=19.14 EndZ=0
    g4: LineSegment StartX=2.76 StartY=19.14 StartZ=0 EndX=3.76 EndY=19.14 EndZ=0
    g5: LineSegment StartX=6.76 StartY=34.14 StartZ=0 EndX=6.76 EndY=19.14 EndZ=0
    g6: LineSegment StartX=6.76 StartY=19.14 StartZ=0 EndX=5.76 EndY=19.14 EndZ=0
    g7: LineSegment StartX=5.76 StartY=34.14 StartZ=0 EndX=5.76 EndY=19.14 EndZ=0
    g8: LineSegment StartX=6.76 StartY=34.14 StartZ=0 EndX=5.76 EndY=34.14 EndZ=0
  constraints (27):
    c: Vertical(g0)
    c: PointOnObject(g0,g-3)
    c: Distance(g0,g-4) = 3.36
    c: Distance(g1) = 1
    c: Horizontal(g1)
    c: PointOnObject(g1,g-3)
    c: Vertical(g2)
    c: Coincident(g2,g1)
    c: Distance(g3) = 15
    c: Vertical(g3)
    c: Coincident(g3,g1)
    c: Coincident(g4,g2)
    c: Coincident(g4,g3)
    c: Equal(g0,g3)
    c: Equal(g3,g2)
    c: Distance(g0,g3) = 1
    c: Distance(g8) = 1
    c: Horizontal(g8)
    c: Vertical(g5)
    c: Coincident(g5,g8)
    c: Distance(g7) = 15
    c: Vertical(g7)
    c: Coincident(g7,g8)
    c: Coincident(g6,g5)
    c: Coincident(g6,g7)
    c: Equal(g7,g5)
    c: Symmetric(g6,g3,g0)
FEATURE [PartDesign::Pad] Pad007
  BaseFeature = -> Pad006
  Direction = (-1,0,0)
  Length = 2.66
  Length2 = 10
  Profile = -> Sketch013
  ReferenceAxis = -> Sketch013 [N_Axis]
  Refine = true
  Suppressed = false
  Type = 0
FEATURE [PartDesign::Plane] DatumPlane
  AttachmentOffset = pos=(0,0,53.5) rot=(0,0,1;0rad)
  AttachmentSupport = -> [Sketch013]
  Length = 91.037
  MapMode = 4
  Placement = pos=(28.6,-53.5,0) rot=(0.57735,-0.57735,0.57735;2.0944rad)
  ResizeMode = 0
  Width = 103.902
FEATURE [PartDesign::Mirrored] Mirrored006
  BaseFeature = -> Pad007
  MirrorPlane = -> DatumPlane
  Originals = -> [Pad007]
  Refine = true
  Suppressed = false
  TransformMode = 0
FEATURE [Sketcher::SketchObject] Sketch014
  ArcFitTolerance = 1e-06
  AttachmentSupport = -> [Mirrored006]
  ExternalGeometry = -> [Mirrored006]
  FullyConstrained = true
  MakeInternals = false
  MapMode = 5
  Placement = pos=(-28.6,0,0) rot=(0.57735,0.57735,0.57735;2.0944rad)
  sketch-geometry (16):
    g0: LineSegment StartX=-104.24 StartY=34.14 StartZ=0 EndX=-103.24 EndY=34.14 EndZ=0
    g1: LineSegment StartX=-104.24 StartY=34.14 StartZ=0 EndX=-104.24 EndY=19.14 EndZ=0
    g2: LineSegment StartX=-104.24 StartY=19.14 StartZ=0 EndX=-103.24 EndY=19.14 EndZ=0
    g3: LineSegment StartX=-103.24 StartY=19.14 StartZ=0 EndX=-103.24 EndY=34.14 EndZ=0
    g4: LineSegment StartX=-101.24 StartY=34.14 StartZ=0 EndX=-100.24 EndY=34.14 EndZ=0
    g5: LineSegment StartX=-101.24 StartY=34.14 StartZ=0 EndX=-101.24 EndY=19.14 EndZ=0
    g6: LineSegment StartX=-101.24 StartY=19.14 StartZ=0 EndX=-100.24 EndY=19.14 EndZ=0
    g7: LineSegment StartX=-100.24 StartY=19.14 StartZ=0 EndX=-100.24 EndY=34.14 EndZ=0
    g8: LineSegment StartX=-6.76 StartY=34.14 StartZ=0 EndX=-5.76 EndY=34.14 EndZ=0
    g9: LineSegment StartX=-6.76 StartY=34.14 StartZ=0 EndX=-6.76 EndY=19.14 EndZ=0
    g10: LineSegment StartX=-6.76 StartY=19.14 StartZ=0 EndX=-5.76 EndY=19.14 EndZ=0
    g11: LineSegment StartX=-5.76 StartY=19.14 StartZ=0 EndX=-5.76 EndY=34.14 EndZ=0
    g12: LineSegment StartX=-3.76 StartY=34.14 StartZ=0 EndX=-2.76 EndY=34.14 EndZ=0
    g13: LineSegment StartX=-3.76 StartY=34.14 StartZ=0 EndX=-3.76 EndY=19.14 EndZ=0
    g14: LineSegment StartX=-3.76 StartY=19.14 StartZ=0 EndX=-2.76 EndY=19.14 EndZ=0
    g15: LineSegment StartX=-2.76 StartY=19.14 StartZ=0 EndX=-2.76 EndY=34.14 EndZ=0
  constraints (32):
    c: Coincident(g0,g-6)
    c: Coincident(g0,g-6)
    c: Coincident(g1,g0)
    c: Coincident(g1,g-5)
    c: Coincident(g2,g1)
    c: Coincident(g2,g-4)
    c: Coincident(g3,g2)
    c: Coincident(g3,g0)
    c: Coincident(g4,g-9)
    c: Coincident(g4,g-8)
    c: Coincident(g5,g4)
    c: Coincident(g5,g-10)
    c: Coincident(g6,g5)
    c: Coincident(g6,g-10)
    c: Coincident(g7,g6)
    c: Coincident(g7,g4)
    c: Coincident(g8,g-14)
    c: Coincident(g8,g-14)
    c: Coincident(g9,g8)
    c: Coincident(g9,g-13)
    c: Coincident(g10,g9)
    c: Coincident(g10,g-12)
    c: Coincident(g11,g10)
    c: Coincident(g11,g8)
    c: Coincident(g12,g-17)
    c: Coincident(g12,g-16)
    c: Coincident(g13,g12)
    c: Coincident(g13,g-18)
    c: Coincident(g14,g13)
    c: Coincident(g14,g-18)
    c: Coincident(g15,g14)
    c: Coincident(g15,g12)
FEATURE [PartDesign::Pad] Pad008
  BaseFeature = -> Mirrored006
  Direction = (1,0,0)
  Length = 2.66
  Length2 = 10
  Profile = -> Sketch014
  ReferenceAxis = -> Sketch014 [N_Axis]
  Refine = true
  Suppressed = false
  Type = 0
FEATURE [PartDesign::Fillet] Fillet003
  Base = -> Pad008 [Edge379,Edge371,Edge373]
  BaseFeature = -> Pad008
  Radius = 2
  Refine = true
  SupportTransform = false
  Suppressed = false
  UseAllEdges = false
FEATURE [PartDesign::Body] Body001
  AllowCompound = false
  Group = -> [Sketch,Pad,Thickness,Thickness001,Sketch001,Pocket,Sketch002,Pad001,Sketch003,Pad002,Sketch004,Pad003,Sketch005,Pad004,Mirrored,Sketch006,Pocket001,Mirrored001,Sketch007,Pocket002,Mirrored002,Fillet,Mirrored003,Sketch008,Pocket003,Sketch009,Pocket004,Mirrored004,Fillet001,Sketch010,Pocket005,Fillet002,Sketch011,Pad005,Mirrored005,Sketch012,Pad006,Sketch013,Pad007,DatumPlane,Mirrored006,Sketch014,+2 more]
  Origin = -> Origin001
  Tip = -> Fillet003
